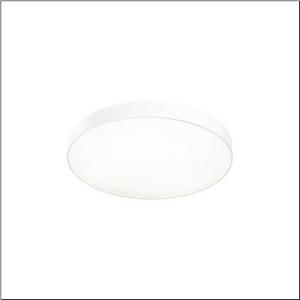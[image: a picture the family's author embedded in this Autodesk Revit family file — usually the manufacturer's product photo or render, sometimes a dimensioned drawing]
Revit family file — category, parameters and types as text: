
# Revit family: round_21_m_51mr36fd0421w
name_source: partatom
category: Lighting Fixtures
units: mm (PartAtom-declared; Revit-internal decimal feet)

## family parameters
Cut with Voids When Loaded = No
Host = Face
Light Source = No
Part Type = Normal
Room Calculation Point = No
Round Connector Dimension = Use Diameter
Shared = No

## types (1)
- Round 21 M (1 x LED, 7810 lm, 54.9 W, 4000K)
    Apparent Load = 55 VA
    CIE Flux Codes = 49 80 96 100 100
    Color Rendering = 80
    Color Temperature = 4000K
    Default Elevation = 1800 mm
    Description = Round 21 M, wall and ceiling luminaire, primary optical cover: cover, of PMMA, opal, light emission: direct distribution, primary light characteristic: symmetric, installation type: surface-mounted, suspended mounting, LED, rated luminous flux: 7.810lm, luminous efficacy: 142lm/W, light colour: 840, colour temperature: 4000K, control gear: DALI 2, with terminal, 5-pole, mains connection: 230V, AC, 50/60Hz, rated input power: 55W, housing, of aluminium, coated, white, diameter: 600mm, height: 62mm, protection rating (complete): IP40, insulation class (complete): insulation class I (protective earthing), certification: CE, impact resistance: IK04, permissible operating ambient temperature: -10..+35°C, packaging unit: 1 piece
    Height = 87 mm
    Lamp = 1 x LED
    Lamp Light Flux = 7810 lm
    Lamp Power = 54.9 W
    Lamp count = 1
    Length = 600 mm
    Luminous efficacy = 142 lm/W
    Manufacturer = Siteco
    ModVariant = No
    Model = 51MR36FD0421W
    Mounting Place = Ceiling
    Mounting Type = Surface mounted
    Number of Poles = 1
    OnlyDefault = Yes
    Power Factor = 1
    Product Name = Round 21 M
    Product group = wall and ceiling luminaire | ceiling mounted
    ProductGroupID = 304
    Protection Class = Protection class I
    Protection Degree = IP 40
    RLX_Detail_Level = 1
    RLX_Emergency_Light_Flux = 0 lm
    RLX_Emergency_Type = 0
    RLX_Emergency_Type_DB = No
    RlxData = <blob elided: 11729 chars, md5=e6ffcaef>
    Socket = socket
    Standby Power = 0 W
    System Light Flux = 7810 lm
    System Power = 55 W
    Type Comments = Product without accessories
    Type Image = l_1258330.jpg
    URL = http://relux.com
    VarID = ---
    Voltage = 0 V
    Weight = 0.00 kg
    Width = 0 mm  [stored 0 ft]

note: [stored X ft] marks values corroborated as IEEE doubles in the binary element streams (Revit-internal decimal feet)

## geometry (parser evidence)
native form markers: Sweep x10
no freeform markers — native parametric forms only
